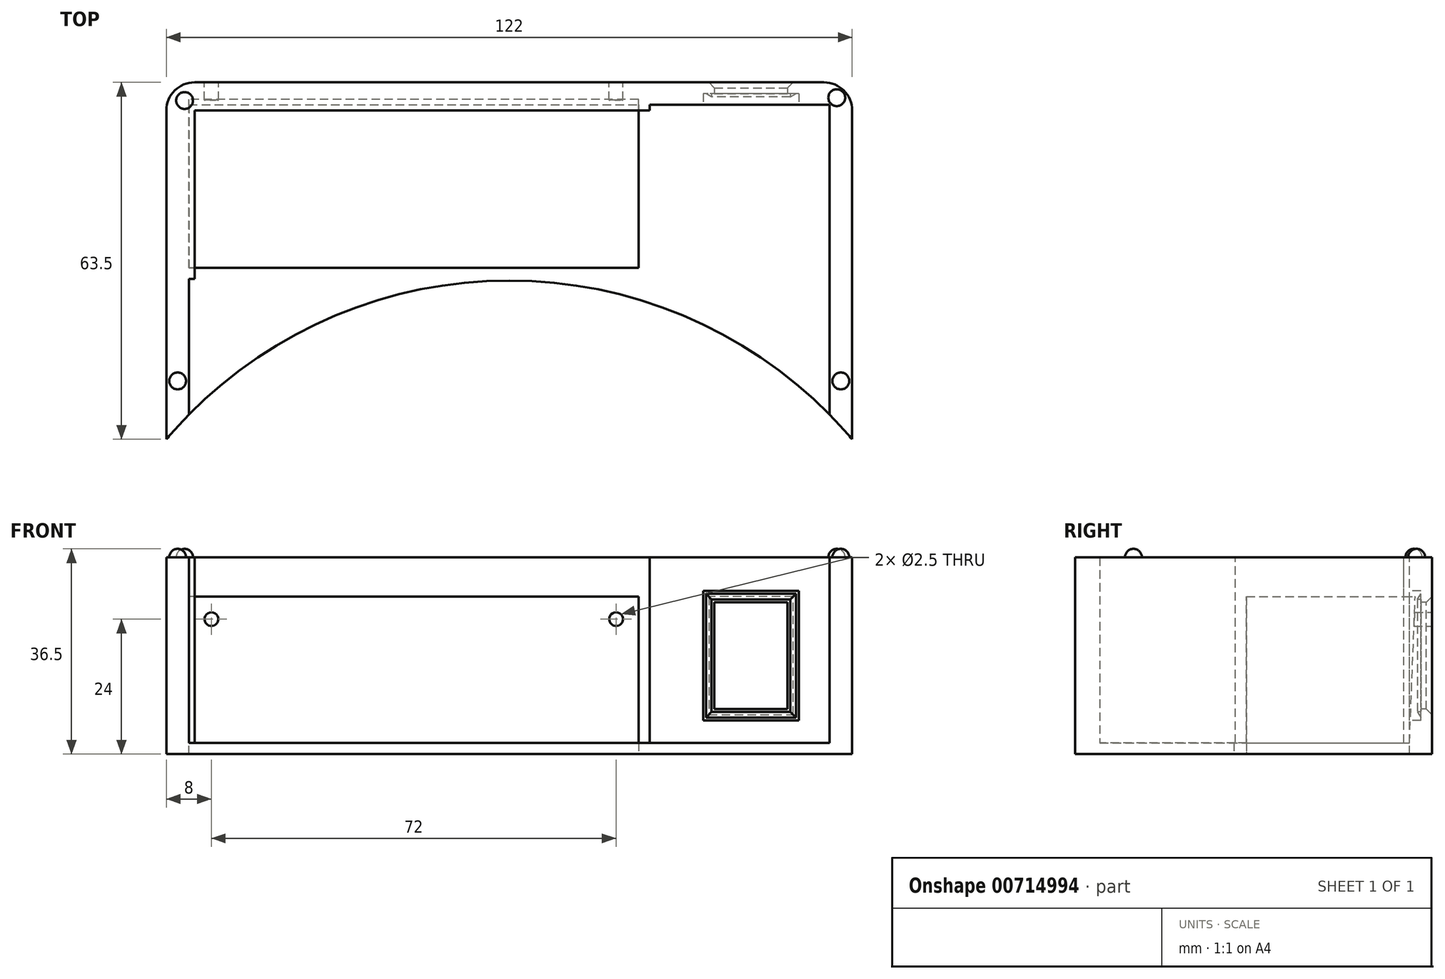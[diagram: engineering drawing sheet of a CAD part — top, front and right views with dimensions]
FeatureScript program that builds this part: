
annotation { "Feature Type Name" : "Feature", "Feature Type Description" : "" }
export const myFeature = defineFeature(function(context is Context, id is Id, definition is map)
    precondition{}
    {
        {
            var Q0;
            Q0=qCreatedBy(makeId("Top.planeOp"),FACE);
            var sketch = newSketch(context, id + "F0", { "sketchPlane" : qUnion([Q0])});
            skLineSegment(sketch, "E0.bottom", {"start": v(61, 31.75) * mm, "end": v(-61, 31.75) * mm});
            skLineSegment(sketch, "E0.top", {"start": v(61, -31.75) * mm, "end": v(-61, -31.75) * mm});
            skLineSegment(sketch, "E0.left", {"start": v(61, 31.75) * mm, "end": v(61, -31.75) * mm});
            skLineSegment(sketch, "E0.right", {"start": v(-61, 31.75) * mm, "end": v(-61, -31.75) * mm});
            skPoint(sketch, "E0.middle", {"position": v(0, 0) * mm});
            skSolve(sketch);
        }
        {
            var Q0;
            Q0=makeQuery(id+"F0.imprint","IMPRINT",FACE,{"disambiguationData":[TD([[makeQuery(id+"F0.imprint","IMPRINT",EDGE,{"derivedFrom":sQuery(id+"F0.wireOp",EDGE,"E0.bottom")}),1.0]])]});
            extrude(context, id + "F1", {"entities" : qUnion([Q0]), "depth" : 35 * mm, "offsetDistance" : 25 * mm});
        }
        {
            var Q0;
            Q0=makeQuery(id+"F1.opExtrude","CAP_FACE",FACE,{"disambiguationData":[OSD([sQuery(id+"F0.wireOp",EDGE,"E0.bottom"),sQuery(id+"F0.wireOp",EDGE,"E0.top"),sQuery(id+"F0.wireOp",EDGE,"E0.left"),sQuery(id+"F0.wireOp",EDGE,"E0.right")])],"isStart":false});
            var sketch = newSketch(context, id + "F2", { "sketchPlane" : qUnion([Q0])});
            skLineSegment(sketch, "E1.0", {"start": v(-57, -27.75) * mm, "end": v(57, -27.75) * mm});
            skLineSegment(sketch, "E1.1", {"start": v(-57, 27.75) * mm, "end": v(-57, -27.75) * mm});
            skLineSegment(sketch, "E1.2", {"start": v(57, 27.75) * mm, "end": v(-57, 27.75) * mm});
            skLineSegment(sketch, "E1.3", {"start": v(57, -27.75) * mm, "end": v(57, 27.75) * mm});
            skSolve(sketch);
        }
        {
            var Q0;
            Q0=makeQuery(id+"F2.imprint","IMPRINT",FACE,{"disambiguationData":[TD([[makeQuery(id+"F2.imprint","IMPRINT",EDGE,{"derivedFrom":sQuery(id+"F2.wireOp",EDGE,"E1.0")}),1.0]])]});
            extrude(context, id + "F3", {"entities" : qUnion([Q0]), "operationType" : NewBodyOperationType.REMOVE, "oppositeDirection" : true, "depth" : 33 * mm, "offsetDistance" : 25 * mm});
        }
        {
            var Q0;
            Q0=makeQuery(id+"F1.opExtrude","CAP_FACE",FACE,{"disambiguationData":[OSD([sQuery(id+"F0.wireOp",EDGE,"E0.bottom"),sQuery(id+"F0.wireOp",EDGE,"E0.top"),sQuery(id+"F0.wireOp",EDGE,"E0.left"),sQuery(id+"F0.wireOp",EDGE,"E0.right")])],"isStart":true});
            var sketch = newSketch(context, id + "F4", { "sketchPlane" : qUnion([Q0])});
            skLineSegment(sketch, "E2.bottom", {"start": v(-61, -31.75) * mm, "end": v(-57, -31.75) * mm, "construction": true});
            skLineSegment(sketch, "E2.top", {"start": v(-61, 31.75) * mm, "end": v(-57, 31.75) * mm, "construction": true});
            skLineSegment(sketch, "E2.left", {"start": v(-61, -31.75) * mm, "end": v(-61, 31.75) * mm, "construction": true});
            skLineSegment(sketch, "E2.right", {"start": v(-57, -31.75) * mm, "end": v(-57, 31.75) * mm, "construction": true});
            skLineSegment(sketch, "E3.bottom", {"start": v(-61, -31.75) * mm, "end": v(61, -31.75) * mm, "construction": true});
            skLineSegment(sketch, "E3.top", {"start": v(-61, -27.75) * mm, "end": v(61, -27.75) * mm, "construction": true});
            skLineSegment(sketch, "E3.left", {"start": v(-61, -31.75) * mm, "end": v(-61, -27.75) * mm, "construction": true});
            skLineSegment(sketch, "E3.right", {"start": v(61, -31.75) * mm, "end": v(61, -27.75) * mm, "construction": true});
            skLineSegment(sketch, "E4.bottom", {"start": v(-57, -27.75) * mm, "end": v(23, -27.75) * mm});
            skLineSegment(sketch, "E4.top", {"start": v(-57, 1.25) * mm, "end": v(23, 1.25) * mm});
            skLineSegment(sketch, "E4.left", {"start": v(-57, -27.75) * mm, "end": v(-57, 1.25) * mm});
            skLineSegment(sketch, "E4.right", {"start": v(23, -27.75) * mm, "end": v(23, 1.25) * mm});
            skSolve(sketch);
        }
        {
            var Q0;
            Q0=makeQuery(id+"F4.imprint","IMPRINT",FACE,{"disambiguationData":[TD([[makeQuery(id+"F4.imprint","IMPRINT",EDGE,{"derivedFrom":sQuery(id+"F4.wireOp",EDGE,"E4.bottom")}),1.0]])]});
            extrude(context, id + "F5", {"entities" : qUnion([Q0]), "operationType" : NewBodyOperationType.REMOVE, "endBound" : BoundingType.THROUGH_ALL, "oppositeDirection" : true, "depth" : 25 * mm, "offsetDistance" : 25 * mm});
        }
        {
            var Q0;
            Q0=makeQuery(id+"F5.boolean.opBoolean","MERGE",FACE,{"derivedFrom":[makeQuery(id+"F3.boolean.opBoolean","COPY",FACE,{"derivedFrom":makeQuery(id+"F3.opExtrude","SWEPT_FACE",FACE,{"disambiguationData":[OSD([sQuery(id+"F2.wireOp",EDGE,"E1.2")])]})}),makeQuery(id+"F5.opExtrude","SWEPT_FACE",FACE,{"disambiguationData":[OSD([sQuery(id+"F4.wireOp",EDGE,"E4.bottom")])]})]});
            var sketch = newSketch(context, id + "F6", { "sketchPlane" : qUnion([Q0])});
            skLineSegment(sketch, "E5.bottom", {"start": v(23, 2) * mm, "end": v(25, 2) * mm});
            skLineSegment(sketch, "E5.top", {"start": v(23, 35) * mm, "end": v(25, 35) * mm});
            skLineSegment(sketch, "E5.left", {"start": v(23, 2) * mm, "end": v(23, 28) * mm});
            skLineSegment(sketch, "E5.right", {"start": v(25, 2) * mm, "end": v(25, 35) * mm});
            skLineSegment(sketch, "E6.bottom", {"start": v(23, 35) * mm, "end": v(-57, 35) * mm});
            skLineSegment(sketch, "E6.top", {"start": v(23, 28) * mm, "end": v(-57, 28) * mm});
            skLineSegment(sketch, "E6.right", {"start": v(-57, 35) * mm, "end": v(-57, 28) * mm});
            skLineSegment(sketch, "E7", {"start": v(23, 28) * mm, "end": v(23, 35) * mm, "construction": true});
            skSolve(sketch);
        }
        {
            var Q0;
            Q0=makeQuery(id+"F6.imprint","IMPRINT",FACE,{"disambiguationData":[TD([[makeQuery(id+"F6.imprint","IMPRINT",EDGE,{"derivedFrom":sQuery(id+"F6.wireOp",EDGE,"E5.bottom")}),-1.0]])]});
            extrude(context, id + "F7", {"entities" : qUnion([Q0]), "operationType" : NewBodyOperationType.ADD, "depth" : 1 * mm, "offsetDistance" : 25 * mm});
        }
        {
            var Q0;
            Q0=makeQuery(id+"F7.boolean.opBoolean","SPLIT",FACE,{"disambiguationData":[TD([makeQuery(id+"F3.boolean.opBoolean","COPY",FACE,{"derivedFrom":makeQuery(id+"F3.opExtrude","SWEPT_FACE",FACE,{"disambiguationData":[OSD([sQuery(id+"F2.wireOp",EDGE,"E1.1")])]})})])],"derivedFrom":makeQuery(id+"F5.boolean.opBoolean","MERGE",FACE,{"derivedFrom":[makeQuery(id+"F3.boolean.opBoolean","COPY",FACE,{"derivedFrom":makeQuery(id+"F3.opExtrude","SWEPT_FACE",FACE,{"disambiguationData":[OSD([sQuery(id+"F2.wireOp",EDGE,"E1.2")])]})}),makeQuery(id+"F5.opExtrude","SWEPT_FACE",FACE,{"disambiguationData":[OSD([sQuery(id+"F4.wireOp",EDGE,"E4.bottom")])]})]})});
            var sketch = newSketch(context, id + "F8", { "sketchPlane" : qUnion([Q0])});
            skLineSegment(sketch, "E8.bottom", {"start": v(-57, 0) * mm, "end": v(23, 0) * mm, "construction": true});
            skLineSegment(sketch, "E8.top", {"start": v(-57, 2) * mm, "end": v(23, 2) * mm, "construction": true});
            skLineSegment(sketch, "E8.left", {"start": v(-57, 0) * mm, "end": v(-57, 2) * mm, "construction": true});
            skLineSegment(sketch, "E8.right", {"start": v(23, 0) * mm, "end": v(23, 2) * mm, "construction": true});
            skLineSegment(sketch, "E9.bottom", {"start": v(-57, 2) * mm, "end": v(23, 2) * mm});
            skLineSegment(sketch, "E9.top", {"start": v(-57, 28) * mm, "end": v(23, 28) * mm});
            skLineSegment(sketch, "E9.left", {"start": v(-57, 2) * mm, "end": v(-57, 28) * mm});
            skLineSegment(sketch, "E9.right", {"start": v(23, 2) * mm, "end": v(23, 28) * mm});
            skSolve(sketch);
        }
        {
            var Q0;
            Q0=makeQuery(id+"F8.imprint","IMPRINT",FACE,{"disambiguationData":[TD([[makeQuery(id+"F8.imprint","IMPRINT",EDGE,{"derivedFrom":sQuery(id+"F8.wireOp",EDGE,"E9.bottom")}),1.0]])]});
            extrude(context, id + "F9", {"entities" : qUnion([Q0]), "operationType" : NewBodyOperationType.REMOVE, "oppositeDirection" : true, "depth" : 1 * mm, "offsetDistance" : 25 * mm});
        }
        {
            var Q0;
            Q0=makeQuery(id+"F9.boolean.opBoolean","MERGE",FACE,{"derivedFrom":[makeQuery(id+"F7.boolean.opBoolean","MERGE",FACE,{"derivedFrom":[makeQuery(id+"F5.boolean.opBoolean","COPY",FACE,{"derivedFrom":makeQuery(id+"F5.opExtrude","SWEPT_FACE",FACE,{"disambiguationData":[OSD([sQuery(id+"F4.wireOp",EDGE,"E4.right")])]})}),makeQuery(id+"F7.opExtrude","SWEPT_FACE",FACE,{"disambiguationData":[OSD([sQuery(id+"F6.wireOp",EDGE,"E5.left")])]})]}),makeQuery(id+"F9.opExtrude","SWEPT_FACE",FACE,{"disambiguationData":[OSD([sQuery(id+"F8.wireOp",EDGE,"E9.right")])]})]});
            var sketch = newSketch(context, id + "F10", { "sketchPlane" : qUnion([Q0])});
            skLineSegment(sketch, "E10", {"start": v(-27.75, 2) * mm, "end": v(-28.75, 28) * mm});
            skSolve(sketch);
        }
        {
            var Q0;
            Q0=makeQuery(id+"F10.imprint","IMPRINT",FACE,{"disambiguationData":[TD([[makeQuery(id+"F10.imprint","IMPRINT",EDGE,{"derivedFrom":sQuery(id+"F10.wireOp",EDGE,"E10")}),1.0]])]});
            extrude(context, id + "F11", {"entities" : qUnion([Q0]), "operationType" : NewBodyOperationType.ADD, "endBound" : BoundingType.UP_TO_NEXT, "depth" : 25 * mm, "offsetDistance" : 25 * mm});
        }
        {
            var Q0;
            Q0=makeQuery(id+"F9.boolean.opBoolean","MERGE",FACE,{"derivedFrom":[makeQuery(id+"F5.boolean.opBoolean","MERGE",FACE,{"derivedFrom":[makeQuery(id+"F3.boolean.opBoolean","COPY",FACE,{"derivedFrom":makeQuery(id+"F3.opExtrude","SWEPT_FACE",FACE,{"disambiguationData":[OSD([sQuery(id+"F2.wireOp",EDGE,"E1.1")])]})}),makeQuery(id+"F5.opExtrude","SWEPT_FACE",FACE,{"disambiguationData":[OSD([sQuery(id+"F4.wireOp",EDGE,"E4.left")])]})]}),makeQuery(id+"F9.opExtrude","SWEPT_FACE",FACE,{"disambiguationData":[OSD([sQuery(id+"F8.wireOp",EDGE,"E9.left")])]})]});
            var sketch = newSketch(context, id + "F12", { "sketchPlane" : qUnion([Q0])});
            skLineSegment(sketch, "E11.bottom", {"start": v(-1.25, 2) * mm, "end": v(-3.25, 2) * mm});
            skLineSegment(sketch, "E11.top", {"start": v(-1.25, 35) * mm, "end": v(-3.25, 35) * mm});
            skLineSegment(sketch, "E11.left", {"start": v(-1.25, 2) * mm, "end": v(-1.25, 28) * mm});
            skLineSegment(sketch, "E11.right", {"start": v(-3.25, 2) * mm, "end": v(-3.25, 35) * mm});
            skLineSegment(sketch, "E12.bottom", {"start": v(-1.25, 35) * mm, "end": v(26.75, 35) * mm});
            skLineSegment(sketch, "E12.top", {"start": v(-1.25, 28) * mm, "end": v(26.75, 28) * mm});
            skLineSegment(sketch, "E12.right", {"start": v(26.75, 35) * mm, "end": v(26.75, 28) * mm});
            skSolve(sketch);
        }
        {
            var Q0;
            Q0=makeQuery(id+"F12.imprint","IMPRINT",FACE,{"disambiguationData":[TD([[makeQuery(id+"F12.imprint","IMPRINT",EDGE,{"derivedFrom":sQuery(id+"F12.wireOp",EDGE,"E11.bottom")}),-1.0]])]});
            extrude(context, id + "F13", {"entities" : qUnion([Q0]), "operationType" : NewBodyOperationType.ADD, "depth" : 1 * mm, "offsetDistance" : 25 * mm});
        }
        {
            var Q0;
            Q0=makeQuery(id+"F1.opExtrude","CAP_FACE",FACE,{"disambiguationData":[OSD([sQuery(id+"F0.wireOp",EDGE,"E0.bottom"),sQuery(id+"F0.wireOp",EDGE,"E0.top"),sQuery(id+"F0.wireOp",EDGE,"E0.left"),sQuery(id+"F0.wireOp",EDGE,"E0.right")])],"isStart":true});
            var sketch = newSketch(context, id + "F14", { "sketchPlane" : qUnion([Q0])});
            skPoint(sketch, "E13.oppositeSnap0", {"position": v(0, 31.75) * mm});
            skLineSegment(sketch, "E13.bottom", {"start": v(61, 31.75) * mm, "end": v(0, 31.75) * mm, "construction": true});
            skLineSegment(sketch, "E13.top", {"start": v(61, 83.5) * mm, "end": v(0, 83.5) * mm, "construction": true});
            skLineSegment(sketch, "E13.left", {"start": v(61, 31.75) * mm, "end": v(61, 83.5) * mm, "construction": true});
            skLineSegment(sketch, "E13.right", {"start": v(0, 31.75) * mm, "end": v(0, 83.5) * mm, "construction": true});
            skCircle(sketch, "E14", {"center": v(0, 83.5) * mm, "radius": 80 * mm});
            skSolve(sketch);
        }
        {
            var Q0;
            Q0 = qSketchRegion(id + "F14", true);
            var Q1;
            {var subQ1=makeQuery(id+"F1.opExtrude","CAP_EDGE",EDGE,{"disambiguationData":[OSD([sQuery(id+"F0.wireOp",EDGE,"E0.top")])],"isStart":true});Q1=makeQuery(id+"F14.imprint","IMPRINT",FACE,{"disambiguationData":[TD([[makeQuery(id+"F14.imprint","IMPRINT",EDGE,{"derivedFrom":subQ1}),1.0]])]});}
            extrude(context, id + "F15", {"entities" : qUnion([Q0, Q1]), "operationType" : NewBodyOperationType.REMOVE, "endBound" : BoundingType.THROUGH_ALL, "oppositeDirection" : true, "depth" : 25 * mm, "offsetDistance" : 25 * mm});
        }
        {
            var Q0;
            Q0=makeQuery(id+"F1.opExtrude","SWEPT_FACE",FACE,{"disambiguationData":[OSD([sQuery(id+"F0.wireOp",EDGE,"E0.bottom")])]});
            var sketch = newSketch(context, id + "F16", { "sketchPlane" : qUnion([Q0])});
            skLineSegment(sketch, "E15.bottom", {"start": v(61, 35) * mm, "end": v(-23, 35) * mm, "construction": true});
            skLineSegment(sketch, "E15.top", {"start": v(61, 0) * mm, "end": v(-23, 0) * mm, "construction": true});
            skLineSegment(sketch, "E15.left", {"start": v(61, 35) * mm, "end": v(61, 0) * mm, "construction": true});
            skLineSegment(sketch, "E15.right", {"start": v(-23, 35) * mm, "end": v(-23, 0) * mm, "construction": true});
            skLineSegment(sketch, "E16.bottom", {"start": v(61, 35) * mm, "end": v(53, 35) * mm, "construction": true});
            skLineSegment(sketch, "E16.top", {"start": v(61, 0) * mm, "end": v(53, 0) * mm, "construction": true});
            skLineSegment(sketch, "E16.right", {"start": v(53, 35) * mm, "end": v(53, 0) * mm, "construction": true});
            skLineSegment(sketch, "E17.bottom", {"start": v(-23, 35) * mm, "end": v(-19, 35) * mm, "construction": true});
            skLineSegment(sketch, "E17.top", {"start": v(-23, 0) * mm, "end": v(-19, 0) * mm, "construction": true});
            skLineSegment(sketch, "E17.right", {"start": v(-19, 35) * mm, "end": v(-19, 0) * mm, "construction": true});
            skLineSegment(sketch, "E18", {"start": v(-19, 35) * mm, "end": v(-19, 24) * mm, "construction": true});
            skLineSegment(sketch, "E19", {"start": v(53, 35) * mm, "end": v(53, 24) * mm, "construction": true});
            skSolve(sketch);
        }
        {
            var Q0;
            Q0=sQuery(id+"F16.wireOp",VERTEX,"E18.end");
            var Q1;
            Q1=sQuery(id+"F16.wireOp",VERTEX,"E19.end");
            var Q2;
            Q2=makeQuery(id+"F1.opExtrude","SWEPT_BODY",BODY,{"disambiguationData":[OSD([sQuery(id+"F0.wireOp",EDGE,"E0.bottom"),sQuery(id+"F0.wireOp",EDGE,"E0.top"),sQuery(id+"F0.wireOp",EDGE,"E0.left"),sQuery(id+"F0.wireOp",EDGE,"E0.right")])]});
            hole(context, id + "F17", {"style" : HoleStyle.SIMPLE, "endStyle" : HoleEndStyle.THROUGH, "holeDiameter" : 2.5 * mm, "majorDiameter" : 5 * mm, "isTappedThrough" : true, "tappedDepth" : 12 * mm, "tapClearance" : 3, "startFromSketch" : true, "locations" : qUnion([Q0, Q1]), "scope" : qUnion([Q2])});
        }
        {
            var Q0;
            {var subQ0=sQuery(id+"F2.wireOp",EDGE,"E1.3");var subQ1=sQuery(id+"F2.wireOp",EDGE,"E1.2");Q0=makeQuery(id+"F7.boolean.opBoolean","SPLIT",FACE,{"disambiguationData":[TD([makeQuery(id+"F3.boolean.opBoolean","COPY",FACE,{"derivedFrom":makeQuery(id+"F3.opExtrude","SWEPT_FACE",FACE,{"disambiguationData":[OSD([subQ0])]})})])],"derivedFrom":makeQuery(id+"F5.boolean.opBoolean","MERGE",FACE,{"derivedFrom":[makeQuery(id+"F3.boolean.opBoolean","COPY",FACE,{"derivedFrom":makeQuery(id+"F3.opExtrude","SWEPT_FACE",FACE,{"disambiguationData":[OSD([subQ1])]})}),makeQuery(id+"F5.opExtrude","SWEPT_FACE",FACE,{"disambiguationData":[OSD([sQuery(id+"F4.wireOp",EDGE,"E4.bottom")])]})]})});}
            var sketch = newSketch(context, id + "F18", { "sketchPlane" : qUnion([Q0])});
            skLineSegment(sketch, "E20.bottom", {"start": v(57, 35) * mm, "end": v(51.5, 35) * mm, "construction": true});
            skLineSegment(sketch, "E20.top", {"start": v(57, 2) * mm, "end": v(51.5, 2) * mm, "construction": true});
            skLineSegment(sketch, "E20.left", {"start": v(57, 35) * mm, "end": v(57, 2) * mm, "construction": true});
            skLineSegment(sketch, "E20.right", {"start": v(51.5, 35) * mm, "end": v(51.5, 2) * mm, "construction": true});
            skLineSegment(sketch, "E21.bottom", {"start": v(51.5, 2) * mm, "end": v(34.5, 2) * mm, "construction": true});
            skLineSegment(sketch, "E21.top", {"start": v(51.5, 6) * mm, "end": v(34.5, 6) * mm, "construction": true});
            skLineSegment(sketch, "E21.left", {"start": v(51.5, 2) * mm, "end": v(51.5, 6) * mm, "construction": true});
            skLineSegment(sketch, "E21.right", {"start": v(34.5, 2) * mm, "end": v(34.5, 6) * mm, "construction": true});
            skLineSegment(sketch, "E22.bottom", {"start": v(51.5, 6) * mm, "end": v(34.5, 6) * mm});
            skLineSegment(sketch, "E22.top", {"start": v(51.5, 29) * mm, "end": v(34.5, 29) * mm});
            skLineSegment(sketch, "E22.left", {"start": v(51.5, 6) * mm, "end": v(51.5, 29) * mm});
            skLineSegment(sketch, "E22.right", {"start": v(34.5, 6) * mm, "end": v(34.5, 29) * mm});
            skSolve(sketch);
        }
        {
            var Q0;
            Q0=makeQuery(id+"F18.imprint","IMPRINT",FACE,{"disambiguationData":[TD([[makeQuery(id+"F18.imprint","IMPRINT",EDGE,{"derivedFrom":sQuery(id+"F18.wireOp",EDGE,"E22.bottom")}),-1.0]])]});
            extrude(context, id + "F19", {"entities" : qUnion([Q0]), "operationType" : NewBodyOperationType.REMOVE, "oppositeDirection" : true, "depth" : 2 * mm, "offsetDistance" : 25 * mm});
        }
        {
            var Q0;
            Q0=makeQuery(id+"F19.boolean.opBoolean","COPY",FACE,{"derivedFrom":makeQuery(id+"F19.opExtrude","CAP_FACE",FACE,{"disambiguationData":[OSD([sQuery(id+"F18.wireOp",EDGE,"E22.bottom"),sQuery(id+"F18.wireOp",EDGE,"E22.top"),sQuery(id+"F18.wireOp",EDGE,"E22.left"),sQuery(id+"F18.wireOp",EDGE,"E22.right")])],"isStart":false})});
            var sketch = newSketch(context, id + "F20", { "sketchPlane" : qUnion([Q0])});
            skLineSegment(sketch, "E23.0", {"start": v(51, 6.5) * mm, "end": v(51, 28.5) * mm});
            skLineSegment(sketch, "E23.1", {"start": v(35, 6.5) * mm, "end": v(51, 6.5) * mm});
            skLineSegment(sketch, "E23.2", {"start": v(35, 28.5) * mm, "end": v(35, 6.5) * mm});
            skLineSegment(sketch, "E23.3", {"start": v(51, 28.5) * mm, "end": v(35, 28.5) * mm});
            skSolve(sketch);
        }
        {
            var Q0;
            Q0=makeQuery(id+"F20.imprint","IMPRINT",FACE,{"disambiguationData":[TD([[makeQuery(id+"F20.imprint","IMPRINT",EDGE,{"derivedFrom":sQuery(id+"F20.wireOp",EDGE,"E23.0")}),1.0]])]});
            extrude(context, id + "F21", {"entities" : qUnion([Q0]), "operationType" : NewBodyOperationType.ADD, "depth" : 0.6 * mm, "offsetDistance" : 25 * mm, "hasDraft" : true, "draftAngle" : 59 * degree, "draftPullDirection" : true});
        }
        {
            var Q0;
            Q0=makeQuery(id+"F21.opExtrude","CAP_FACE",FACE,{"disambiguationData":[OSD([sQuery(id+"F20.wireOp",EDGE,"E23.0"),sQuery(id+"F20.wireOp",EDGE,"E23.1"),sQuery(id+"F20.wireOp",EDGE,"E23.2"),sQuery(id+"F20.wireOp",EDGE,"E23.3")])],"isStart":false});
            extrude(context, id + "F22", {"entities" : qUnion([Q0]), "operationType" : NewBodyOperationType.REMOVE, "oppositeDirection" : true, "depth" : 0.6 * mm, "offsetDistance" : 25 * mm});
        }
        {
            var Q0;
            Q0=makeQuery(id+"F22.boolean.opBoolean","COPY",FACE,{"derivedFrom":makeQuery(id+"F22.opExtrude","CAP_FACE",FACE,{"disambiguationData":[OSD([sQuery(id+"F20.wireOp",EDGE,"E23.0"),sQuery(id+"F20.wireOp",EDGE,"E23.1"),sQuery(id+"F20.wireOp",EDGE,"E23.2"),sQuery(id+"F20.wireOp",EDGE,"E23.3")])],"isStart":false})});
            var sketch = newSketch(context, id + "F23", { "sketchPlane" : qUnion([Q0])});
            skLineSegment(sketch, "E24.0", {"start": v(49.5, 8) * mm, "end": v(49.5, 27) * mm});
            skLineSegment(sketch, "E24.1", {"start": v(36.5, 8) * mm, "end": v(49.5, 8) * mm});
            skLineSegment(sketch, "E24.2", {"start": v(36.5, 27) * mm, "end": v(36.5, 8) * mm});
            skLineSegment(sketch, "E24.3", {"start": v(49.5, 27) * mm, "end": v(36.5, 27) * mm});
            skSolve(sketch);
        }
        {
            var Q0;
            Q0 = qSketchRegion(id + "F23", true);
            extrude(context, id + "F24", {"entities" : qUnion([Q0]), "operationType" : NewBodyOperationType.REMOVE, "oppositeDirection" : true, "depth" : 1 * mm, "offsetDistance" : 25 * mm});
        }
        {
            var Q0;
            Q0=makeQuery(id+"F24.boolean.opBoolean","COPY",FACE,{"derivedFrom":makeQuery(id+"F24.opExtrude","CAP_FACE",FACE,{"disambiguationData":[OSD([sQuery(id+"F23.wireOp",EDGE,"E24.0"),sQuery(id+"F23.wireOp",EDGE,"E24.1"),sQuery(id+"F23.wireOp",EDGE,"E24.2"),sQuery(id+"F23.wireOp",EDGE,"E24.3")])],"isStart":false})});
            extrude(context, id + "F25", {"entities" : qUnion([Q0]), "operationType" : NewBodyOperationType.REMOVE, "oppositeDirection" : true, "depth" : 1 * mm, "offsetDistance" : 25 * mm, "hasDraft" : true, "draftAngle" : 45 * degree});
        }
        {
            var Q0;
            Q0=makeQuery(id+"F1.opExtrude","SWEPT_EDGE",EDGE,{"disambiguationData":[OSD([sQuery(id+"F0.wireOp",EDGE,"E0.bottom"),sQuery(id+"F0.wireOp",EDGE,"E0.left")])]});
            var Q1;
            Q1=makeQuery(id+"F1.opExtrude","SWEPT_EDGE",EDGE,{"disambiguationData":[OSD([sQuery(id+"F0.wireOp",EDGE,"E0.bottom"),sQuery(id+"F0.wireOp",EDGE,"E0.right")])]});
            fillet(context, id + "F26", {"entities" : qUnion([Q0, Q1]), "radius" : 5 * mm, "tangentPropagation" : true, "allowEdgeOverflow" : false});
        }
        {
            var Q0;
            Q0=makeQuery(id+"F13.boolean.opBoolean","MERGE",FACE,{"derivedFrom":[makeQuery(id+"F7.boolean.opBoolean","MERGE",FACE,{"derivedFrom":[makeQuery(id+"F1.opExtrude","CAP_FACE",FACE,{"disambiguationData":[OSD([sQuery(id+"F0.wireOp",EDGE,"E0.bottom"),sQuery(id+"F0.wireOp",EDGE,"E0.top"),sQuery(id+"F0.wireOp",EDGE,"E0.left"),sQuery(id+"F0.wireOp",EDGE,"E0.right")])],"isStart":false}),makeQuery(id+"F7.opExtrude","SWEPT_FACE",FACE,{"disambiguationData":[OSD([sQuery(id+"F6.wireOp",EDGE,"E5.top"),sQuery(id+"F6.wireOp",EDGE,"E6.bottom")])]})]}),makeQuery(id+"F13.opExtrude","SWEPT_FACE",FACE,{"disambiguationData":[OSD([sQuery(id+"F12.wireOp",EDGE,"E11.top"),sQuery(id+"F12.wireOp",EDGE,"E12.bottom")])]})]});
            var sketch = newSketch(context, id + "F27", { "sketchPlane" : qUnion([Q0])});
            skLineSegment(sketch, "E25", {"start": v(-56, 26.75) * mm, "end": v(-61, 26.75) * mm, "construction": true});
            skLineSegment(sketch, "E26", {"start": v(-61, 26.75) * mm, "end": v(-56, 31.75) * mm, "construction": true});
            skLineSegment(sketch, "E27", {"start": v(-56, 31.75) * mm, "end": v(-56, 26.75) * mm, "construction": true});
            skLineSegment(sketch, "E28", {"start": v(-56, 26.75) * mm, "end": v(-59.54, 30.29) * mm, "construction": true});
            skCircle(sketch, "E29", {"center": v(-57.77, 28.52) * mm, "radius": 1.5 * mm});
            skLineSegment(sketch, "E30.bottom", {"start": v(-57, -27.38) * mm, "end": v(-61, -27.38) * mm, "construction": true});
            skLineSegment(sketch, "E30.top", {"start": v(-57, -23.38) * mm, "end": v(-61, -23.38) * mm, "construction": true});
            skLineSegment(sketch, "E30.left", {"start": v(-57, -27.38) * mm, "end": v(-57, -23.38) * mm, "construction": true});
            skLineSegment(sketch, "E30.right", {"start": v(-61, -27.38) * mm, "end": v(-61, -23.38) * mm, "construction": true});
            skLineSegment(sketch, "E31.top", {"start": v(-57, -21.38) * mm, "end": v(-61, -21.38) * mm, "construction": true});
            skLineSegment(sketch, "E31.left", {"start": v(-57, -23.38) * mm, "end": v(-57, -21.38) * mm, "construction": true});
            skLineSegment(sketch, "E31.right", {"start": v(-61, -23.38) * mm, "end": v(-61, -21.38) * mm, "construction": true});
            skCircle(sketch, "E32", {"center": v(-59, -21.38) * mm, "radius": 1.5 * mm});
            skLineSegment(sketch, "E33.bottom", {"start": v(57, -27.38) * mm, "end": v(61, -27.38) * mm, "construction": true});
            skLineSegment(sketch, "E33.top", {"start": v(57, -23.38) * mm, "end": v(61, -23.38) * mm, "construction": true});
            skLineSegment(sketch, "E33.left", {"start": v(57, -27.38) * mm, "end": v(57, -23.38) * mm, "construction": true});
            skLineSegment(sketch, "E33.right", {"start": v(61, -27.38) * mm, "end": v(61, -23.38) * mm, "construction": true});
            skLineSegment(sketch, "E34.top", {"start": v(57, -21.38) * mm, "end": v(61, -21.38) * mm, "construction": true});
            skLineSegment(sketch, "E34.left", {"start": v(57, -23.38) * mm, "end": v(57, -21.38) * mm, "construction": true});
            skLineSegment(sketch, "E34.right", {"start": v(61, -23.38) * mm, "end": v(61, -21.38) * mm, "construction": true});
            skCircle(sketch, "E35", {"center": v(59, -21.38) * mm, "radius": 1.5 * mm});
            skLineSegment(sketch, "E36", {"start": v(61, 26.75) * mm, "end": v(57, 27.75) * mm, "construction": true});
            skLineSegment(sketch, "E37", {"start": v(57, 27.75) * mm, "end": v(56, 31.75) * mm, "construction": true});
            skLineSegment(sketch, "E38", {"start": v(56, 31.75) * mm, "end": v(61, 26.75) * mm, "construction": true});
            skLineSegment(sketch, "E39", {"start": v(57, 27.75) * mm, "end": v(59.54, 30.29) * mm, "construction": true});
            skCircle(sketch, "E40", {"center": v(58.27, 29.02) * mm, "radius": 1.5 * mm});
            skSolve(sketch);
        }
        {
            var Q0;
            Q0=makeQuery(id+"F27.imprint","IMPRINT",FACE,{"disambiguationData":[TD([[makeQuery(id+"F27.imprint","IMPRINT",EDGE,{"derivedFrom":sQuery(id+"F27.wireOp",EDGE,"E40")}),1.0]])]});
            var Q1;
            Q1=makeQuery(id+"F27.imprint","IMPRINT",FACE,{"disambiguationData":[TD([[makeQuery(id+"F27.imprint","IMPRINT",EDGE,{"derivedFrom":sQuery(id+"F27.wireOp",EDGE,"E35")}),1.0]])]});
            var Q2;
            Q2=makeQuery(id+"F27.imprint","IMPRINT",FACE,{"disambiguationData":[TD([[makeQuery(id+"F27.imprint","IMPRINT",EDGE,{"derivedFrom":sQuery(id+"F27.wireOp",EDGE,"E32")}),1.0]])]});
            var Q3;
            Q3=makeQuery(id+"F27.imprint","IMPRINT",FACE,{"disambiguationData":[TD([[makeQuery(id+"F27.imprint","IMPRINT",EDGE,{"derivedFrom":sQuery(id+"F27.wireOp",EDGE,"E29")}),1.0]])]});
            extrude(context, id + "F28", {"entities" : qUnion([Q0, Q1, Q2, Q3]), "operationType" : NewBodyOperationType.ADD, "depth" : 1.5 * mm, "offsetDistance" : 25 * mm});
        }
        {
            var Q0;
            Q0=makeQuery(id+"F28.opExtrude","CAP_EDGE",EDGE,{"disambiguationData":[OSD([sQuery(id+"F27.wireOp",EDGE,"E35")])],"isStart":false});
            var Q1;
            Q1=makeQuery(id+"F28.opExtrude","CAP_EDGE",EDGE,{"disambiguationData":[OSD([sQuery(id+"F27.wireOp",EDGE,"E32")])],"isStart":false});
            var Q2;
            Q2=makeQuery(id+"F28.opExtrude","CAP_EDGE",EDGE,{"disambiguationData":[OSD([sQuery(id+"F27.wireOp",EDGE,"E29")])],"isStart":false});
            var Q3;
            Q3=makeQuery(id+"F28.opExtrude","CAP_EDGE",EDGE,{"disambiguationData":[OSD([sQuery(id+"F27.wireOp",EDGE,"E40")])],"isStart":false});
            fillet(context, id + "F29", {"entities" : qUnion([Q0, Q1, Q2, Q3]), "radius" : 1.5 * mm, "tangentPropagation" : true, "allowEdgeOverflow" : false});
        }
    });
